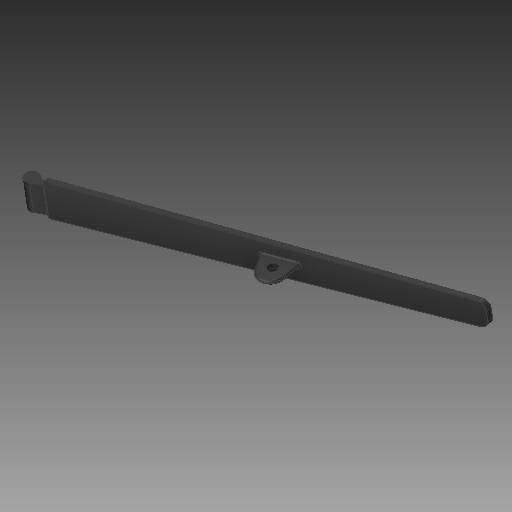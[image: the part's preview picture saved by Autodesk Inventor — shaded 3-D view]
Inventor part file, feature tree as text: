
AUTODESK INVENTOR PART (.ipt)
format: ipt  version: 2019 (Build 230136000, 136)  size: 300,544 bytes
history: native  units: mm
features: fillet x4, other x3
ambient origin geometry x8: Origin, YZ Plane, XZ Plane, XY Plane, X Axis, Y Axis, Z Axis, Center Point
bodies: Solid1 (feature_tree)
feature tree (7):
  other  "BladeSkeleton.ipt"
  fillet  "Fillet1"  Radius=10.0mm
  fillet  "Fillet2"  Radius=3.0mm
  fillet  "Fillet3"  Radius=2.0mm
  fillet  "Fillet4"  Radius=2.0mm
  other  "Solid3::BladeSkeleton.ipt"
  other  "TaggingFeature1"
